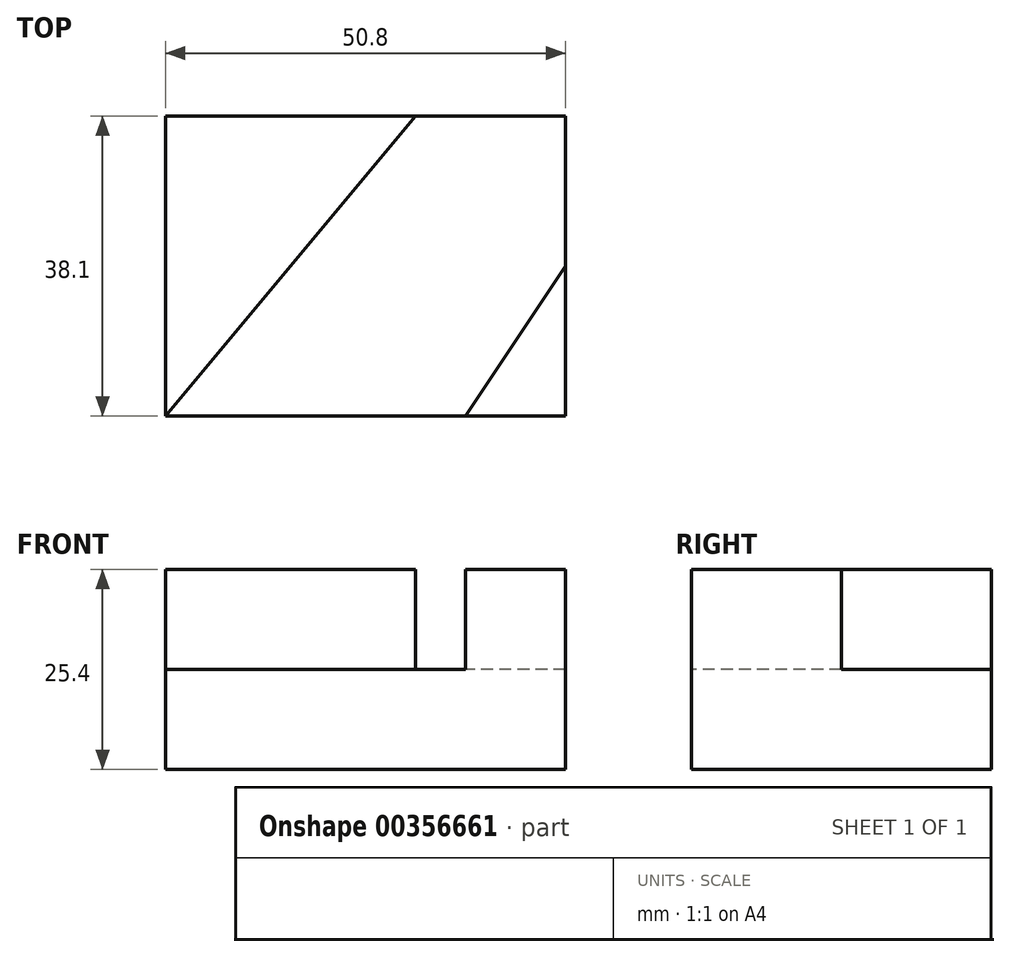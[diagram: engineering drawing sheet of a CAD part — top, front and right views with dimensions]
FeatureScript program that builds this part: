
annotation { "Feature Type Name" : "Feature", "Feature Type Description" : "" }
export const myFeature = defineFeature(function(context is Context, id is Id, definition is map)
    precondition{}
    {
        {
            var Q0;
            Q0=qCreatedBy(makeId("Front.planeOp"),FACE);
            var sketch = newSketch(context, id + "F0", { "sketchPlane" : qUnion([Q0])});
            skLineSegment(sketch, "E0", {"start": v(-32.6, -37.3) * mm, "end": v(18.2, -37.3) * mm});
            skLineSegment(sketch, "E1", {"start": v(18.2, -37.3) * mm, "end": v(18.2, -11.9) * mm});
            skLineSegment(sketch, "E2", {"start": v(18.2, -11.9) * mm, "end": v(-32.6, -11.9) * mm});
            skLineSegment(sketch, "E3", {"start": v(-32.6, -11.9) * mm, "end": v(-32.6, -37.3) * mm});
            skSolve(sketch);
        }
        {
            var Q0;
            Q0=makeQuery(id+"F0.imprint","IMPRINT",FACE,{"disambiguationData":[TD([[makeQuery(id+"F0.imprint","IMPRINT",EDGE,{"derivedFrom":sQuery(id+"F0.wireOp",EDGE,"E0")}),1.0]])]});
            extrude(context, id + "F1", {"entities" : qUnion([Q0]), "depth" : 38.1 * mm});
        }
        {
            var Q0;
            Q0=makeQuery(id+"F1.opExtrude","SWEPT_FACE",FACE,{"disambiguationData":[OSD([sQuery(id+"F0.wireOp",EDGE,"E2")])]});
            var sketch = newSketch(context, id + "F2", { "sketchPlane" : qUnion([Q0])});
            skLineSegment(sketch, "E4", {"start": v(18.2, -19.05) * mm, "end": v(18.2, -38.1) * mm});
            skLineSegment(sketch, "E5", {"start": v(18.2, -38.1) * mm, "end": v(5.5, -38.1) * mm});
            skLineSegment(sketch, "E6", {"start": v(18.2, -19.05) * mm, "end": v(5.5, -38.1) * mm});
            skLineSegment(sketch, "E7", {"start": v(-0.85, 0) * mm, "end": v(-32.6, 0) * mm});
            skLineSegment(sketch, "E8", {"start": v(-32.6, 0) * mm, "end": v(-32.6, -38.1) * mm});
            skLineSegment(sketch, "E9", {"start": v(-32.6, -38.1) * mm, "end": v(-0.85, 0) * mm});
            skSolve(sketch);
        }
        {
            var Q0;
            {var subQ4=sQuery(id+"F2.wireOp",EDGE,"E6");Q0=makeQuery(id+"F2.imprint","IMPRINT",FACE,{"disambiguationData":[TD([[makeQuery(id+"F2.imprint","IMPRINT",EDGE,{"derivedFrom":subQ4}),-1.0]])]});}
            extrude(context, id + "F3", {"entities" : qUnion([Q0]), "operationType" : NewBodyOperationType.REMOVE, "oppositeDirection" : true, "depth" : 12.7 * mm});
        }
    });
